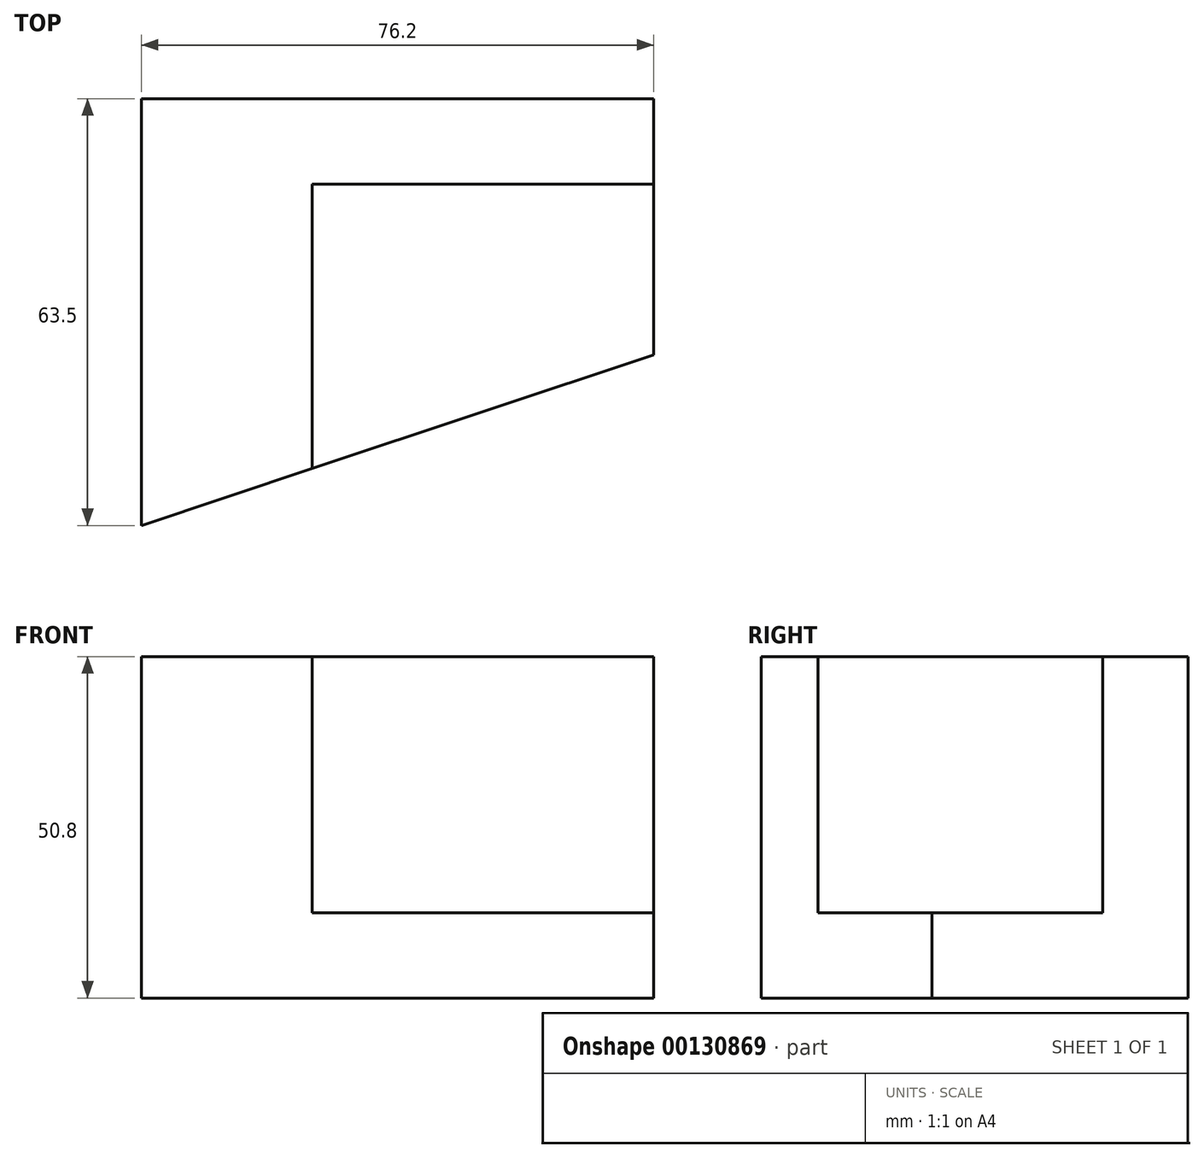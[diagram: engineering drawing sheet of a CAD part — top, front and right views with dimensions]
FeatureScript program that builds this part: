
annotation { "Feature Type Name" : "Feature", "Feature Type Description" : "" }
export const myFeature = defineFeature(function(context is Context, id is Id, definition is map)
    precondition{}
    {
        {
            var Q0;
            Q0=qCreatedBy(makeId("Front.planeOp"),FACE);
            var sketch = newSketch(context, id + "F0", { "sketchPlane" : qUnion([Q0])});
            skLineSegment(sketch, "E0.bottom", {"start": v(-38.1, 0) * mm, "end": v(38.1, 0) * mm});
            skLineSegment(sketch, "E0.top", {"start": v(-38.1, 50.8) * mm, "end": v(38.1, 50.8) * mm});
            skLineSegment(sketch, "E0.left", {"start": v(-38.1, 0) * mm, "end": v(-38.1, 50.8) * mm});
            skLineSegment(sketch, "E0.right", {"start": v(38.1, 0) * mm, "end": v(38.1, 50.8) * mm});
            skSolve(sketch);
        }
        {
            var Q0;
            Q0 = qSketchRegion(id + "F0", true);
            extrude(context, id + "F1", {"entities" : qUnion([Q0]), "oppositeDirection" : true, "depth" : 63.5 * mm});
        }
        {
            var Q0;
            Q0=qCreatedBy(makeId("Front.planeOp"),FACE);
            var sketch = newSketch(context, id + "F2", { "sketchPlane" : qUnion([Q0])});
            skLineSegment(sketch, "E1.bottom", {"start": v(-12.7, 50.8) * mm, "end": v(38.1, 50.8) * mm});
            skLineSegment(sketch, "E1.top", {"start": v(-12.7, 12.7) * mm, "end": v(38.1, 12.7) * mm});
            skLineSegment(sketch, "E1.left", {"start": v(-12.7, 50.8) * mm, "end": v(-12.7, 12.7) * mm});
            skLineSegment(sketch, "E1.right", {"start": v(38.1, 50.8) * mm, "end": v(38.1, 12.7) * mm});
            skSolve(sketch);
        }
        {
            var Q0;
            Q0 = qSketchRegion(id + "F2", true);
            extrude(context, id + "F3", {"entities" : qUnion([Q0]), "operationType" : NewBodyOperationType.REMOVE, "oppositeDirection" : true, "depth" : 50.8 * mm});
        }
        {
            var Q0;
            Q0=qCreatedBy(makeId("Top.planeOp"),FACE);
            var sketch = newSketch(context, id + "F4", { "sketchPlane" : qUnion([Q0])});
            skLineSegment(sketch, "E2", {"start": v(-38.1, 0) * mm, "end": v(38.1, 25.4) * mm});
            skLineSegment(sketch, "E3", {"start": v(38.1, 25.4) * mm, "end": v(38.1, 0) * mm});
            skLineSegment(sketch, "E4", {"start": v(38.1, 0) * mm, "end": v(-38.1, 0) * mm});
            skSolve(sketch);
        }
        {
            var Q0;
            Q0 = qSketchRegion(id + "F4", true);
            extrude(context, id + "F5", {"entities" : qUnion([Q0]), "operationType" : NewBodyOperationType.REMOVE, "endBound" : BoundingType.THROUGH_ALL, "depth" : 25.4 * mm});
        }
    });
